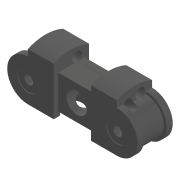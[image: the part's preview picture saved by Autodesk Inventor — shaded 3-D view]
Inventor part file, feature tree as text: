
AUTODESK INVENTOR PART (.ipt)
format: ipt  version: 2020 (Build 240168000, 168)  size: 280,576 bytes
history: native  units: mm
features: extrude x11, sketch x11, plane x3, mirror x2, projected_geometry x2
ambient origin geometry x8: Origin, YZ Plane, XZ Plane, XY Plane, X Axis, Y Axis, Z Axis, Center Point
bodies: Solid1 (feature_tree)
feature tree (29):
  extrude  "Extrusion1"  Depth=9.0mm
  extrude  "Extrusion2"  Depth=3.25mm
  mirror  "Mirror1"
  extrude  "Extrusion3"  Depth=9.25mm
  extrude  "Extrusion4"  Depth=6.25mm TaperAngle=0.0deg
  extrude  "Extrusion5"  Depth=6.25mm TaperAngle=0.0deg
  plane  "Work Plane1"
  extrude  "Extrusion6"  Depth=2.12mm
  extrude  "Extrusion7"  Depth=8.7mm
  plane  "Work Plane2"
  extrude  "Extrusion8"  Depth=5.0mm
  plane  "Work Plane3"
  extrude  "Extrusion9"  Depth=0.65mm
  extrude  "Extrusion10"  Depth=3.0mm
  extrude  "Extrusion11"  Depth=0.2mm
  mirror  "Mirror2"
  sketch  "Sketch1"  dims[d0=9.0mm d1=8.15mm]
  sketch  "Sketch2"  dims[d2=6.4mm d3=0.0mm d4=3.25mm]
  sketch  "Sketch3"  dims[d5=4.25mm d6=9.25mm]
  sketch  "Sketch4"  dims[d8=0.0mm d9=6.25mm d10=0.0mm]
  sketch  "Sketch5"  dims[d11=10.0mm d12=6.25mm d13=0.0mm]
  sketch  "Sketch6"  dims[d14=13.879mm d15=0.0mm d16=2.12mm]
  sketch  "Sketch7"  dims[d17=0.0mm d18=0.0mm d19=8.7mm]
  sketch  "Sketch8"  dims[d20=5.5mm d21=0.0mm d22=5.0mm]
  projected_geometry  "Projected Loop1"
  sketch  "Sketch9"  dims[d23=0.0mm d24=0.0mm d25=0.65mm]
  projected_geometry  "Projected Loop2"
  sketch  "Sketch10"  dims[d26=6.981317mm d27=3.0mm]
  sketch  "Sketch11"  dims[d28=5.5mm d29=0.0mm d30=4.363323mm d31=2.3mm d32=5.5mm d33=11.25mm d34=0.0mm d35=0.0mm d36=2.3mm d37=1.219mm d38=0.0mm d39=5.15mm d40=0.2mm d41=0.0mm]
